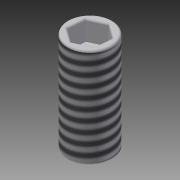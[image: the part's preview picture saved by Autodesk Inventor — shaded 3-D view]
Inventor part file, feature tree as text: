
AUTODESK INVENTOR PART (.ipt)
format: ipt  version: 2014 (Build 180170000, 170)  size: 121,344 bytes
history: native  units: in
note: dims shown in document units (in); Inventor stores cm internally (conversion verified against a paired STEP export)
features: fillet x3, extrude x2, sketch x2, thread x1
ambient origin geometry x8: Origin, YZ Plane, XZ Plane, XY Plane, X Axis, Y Axis, Z Axis, Center Point
bodies: Body1 (feature_tree)
feature tree (8):
  extrude  "Extrusion4"  Depth=0.25in TaperAngle=0.0deg
  thread  "Thread2"  [1 undecoded]
  fillet  "Fillet1"  Radius=0.005in
  extrude  "Extrusion5"  Depth=0.05in TaperAngle=0.0deg
  fillet  "Fillet2"  Radius=0.005in
  fillet  "Fillet3"  Radius=0.005in
  sketch  "Sketch4"  dims[d14=0.112in d15=0.25in d16=0.0in d17=1.0in d18=0.0in d19=0.005in]
  sketch  "Sketch5"  dims[d20=0.05in d21=0.05in d22=0.0in d23=0.005in d24=0.005in]
note: 1 required parameter value undecoded (feature->parameter linkage not recoverable at this tier; creation-order binding heuristic only, values carry confidence <= 0.55)
